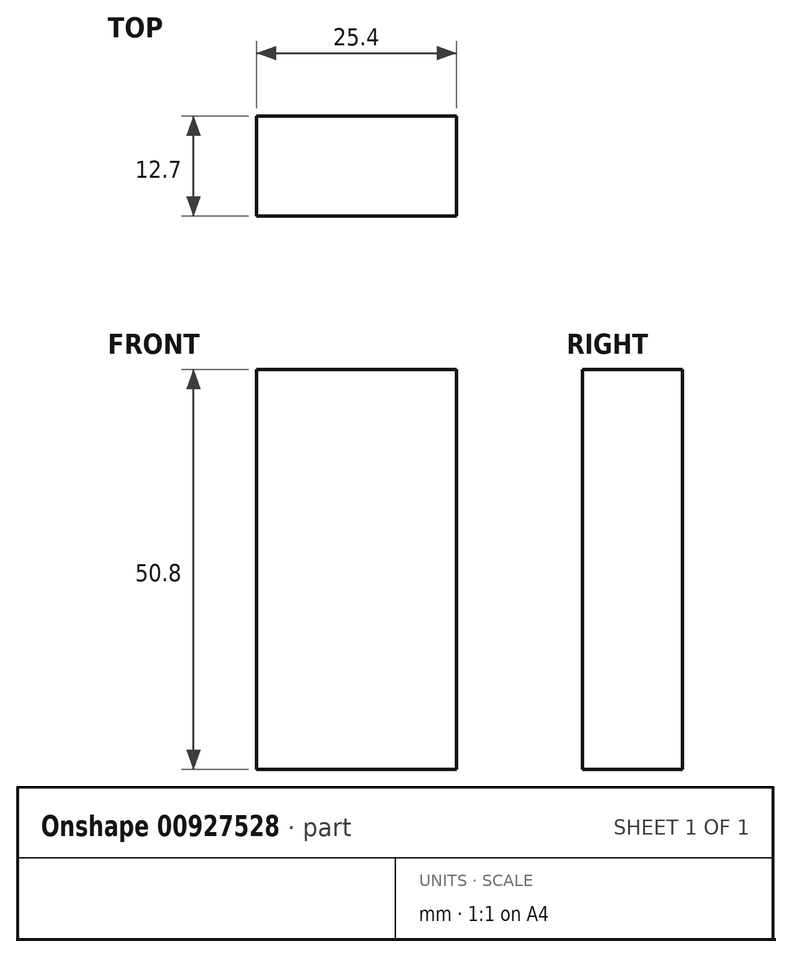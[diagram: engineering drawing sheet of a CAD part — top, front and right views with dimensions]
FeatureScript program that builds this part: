
annotation { "Feature Type Name" : "Feature", "Feature Type Description" : "" }
export const myFeature = defineFeature(function(context is Context, id is Id, definition is map)
    precondition{}
    {
        {
            var Q0;
            Q0=qCreatedBy(makeId("Front.planeOp"),FACE);
            var sketch = newSketch(context, id + "F0", { "sketchPlane" : qUnion([Q0])});
            skLineSegment(sketch, "E0.bottom", {"start": v(-18.72, 15.23) * mm, "end": v(6.68, 15.23) * mm});
            skLineSegment(sketch, "E0.top", {"start": v(-18.72, -35.57) * mm, "end": v(6.68, -35.57) * mm});
            skLineSegment(sketch, "E0.left", {"start": v(-18.72, 15.23) * mm, "end": v(-18.72, -35.57) * mm});
            skLineSegment(sketch, "E0.right", {"start": v(6.68, 15.23) * mm, "end": v(6.68, -35.57) * mm});
            skSolve(sketch);
        }
        {
            var Q0;
            Q0=makeQuery(id+"F0.imprint","IMPRINT",FACE,{"disambiguationData":[TD([[makeQuery(id+"F0.imprint","IMPRINT",EDGE,{"derivedFrom":sQuery(id+"F0.wireOp",EDGE,"E0.bottom")}),-1.0]])]});
            extrude(context, id + "F1", {"entities" : qUnion([Q0]), "depth" : 12.7 * mm, "offsetDistance" : 25.4 * mm});
        }
    });
